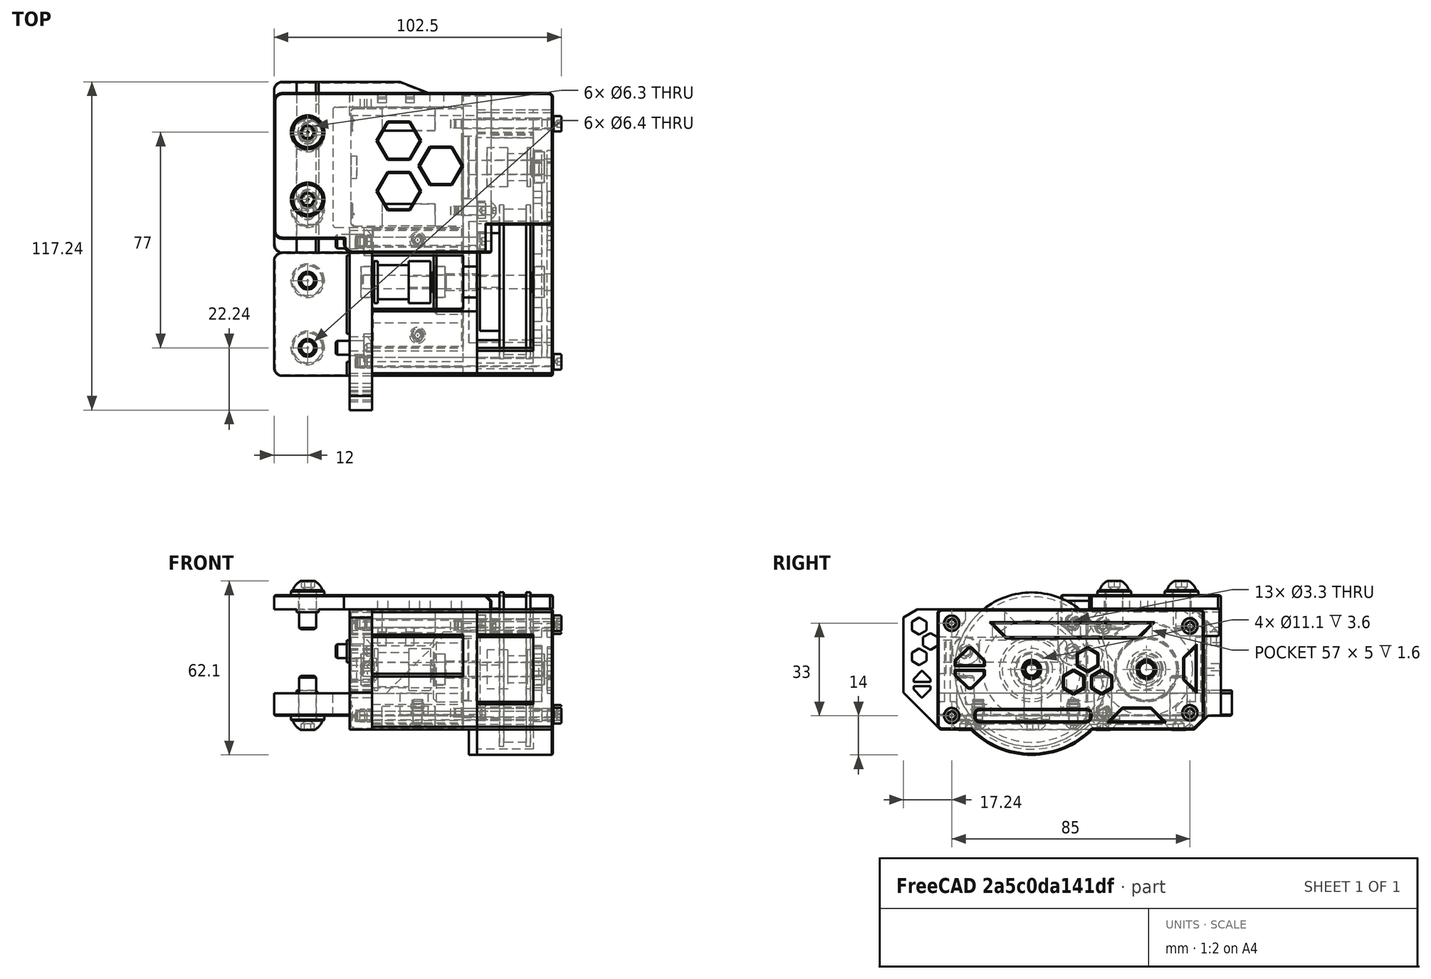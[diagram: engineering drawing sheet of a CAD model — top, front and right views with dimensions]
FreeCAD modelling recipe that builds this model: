
FCSTD DOCUMENT  (FreeCAD 0.19R24291 (Git))
Label: z-motor-left-assembly
License: Other
LicenseURL: GPL3
objects: Part::FeaturePython×28, Part::Feature×18, PartDesign::CoordinateSystem×1, App::Part×1
note: 47 computed .brp shape members not serialized (recipe doc carries the construction recipe); baked Part::Feature solids carry a one-line shape summary decoded from their .brp

FEATURE [Part::Feature] Part__Mirroring014002  label="motor-spacer"
  shape: bbox 0.5 x 6.9 x 6.9 mm, 4 faces (baked)
FEATURE [Part::Feature] Part__Mirroring002001  label="MR115ZZ006"
  shape: bbox 4 x 11 x 11 mm, 4 faces (baked)
FEATURE [Part::Feature] Part__Mirroring004001  label="20t-9mm-pulley001"
  shape: bbox 20 x 15 x 15 mm, 8 faces (baked)
FEATURE [Part::Feature] Part__Mirroring005001  label="MR115ZZ005"
  shape: bbox 4 x 11 x 11 mm, 4 faces (baked)
FEATURE [Part::Feature] Part__Mirroring007001  label="motor-spacer001"
  shape: bbox 0.5 x 6.9 x 6.9 mm, 4 faces (baked)
FEATURE [Part::Feature] Part__Mirroring008001  label="MR115ZZ007"
  shape: bbox 4 x 11 x 11 mm, 4 faces (baked)
FEATURE [Part::Feature] Part__Mirroring009001  label="motor-40mm001"
  shape: bbox 67 x 47 x 42 mm, 100 faces (baked)
FEATURE [Part::Feature] Part__Mirroring011001  label="motor-spacer002"
  shape: bbox 0.5 x 6.9 x 6.9 mm, 4 faces (baked)
FEATURE [Part::Feature] Part__Mirroring012001  label="motor-spacer003"
  shape: bbox 0.5 x 6.9 x 6.9 mm, 4 faces (baked)
FEATURE [Part::Feature] Part__Mirroring014001  label="16t-pulley001"
  shape: bbox 15.5 x 13.9 x 13.9 mm, 8 faces (baked)
FEATURE [Part::FeaturePython] Screw  label="M3x70-Screw"  # Fasteners workbench fastener (typed FeaturePython)
  Placement = pos=(72.5,-69.5,25) rot=(0,1,0;1.5708rad)
  diameter = 4
  invert = true
  length = 10
  lengthCustom = 70
  matchOuter = true
  offset = 0
  thread = false
  type = 33
FEATURE [Part::FeaturePython] Screw001  label="M3x70-Screw001"  # Fasteners workbench fastener (typed FeaturePython)
  Placement = pos=(72.5,-69.5,-8) rot=(0,1,0;1.5708rad)
  diameter = 4
  invert = true
  length = 10
  lengthCustom = 70
  matchOuter = true
  offset = 0
  thread = false
  type = 33
FEATURE [Part::FeaturePython] Screw002  label="M3x35-Screw"  # Fasteners workbench fastener (typed FeaturePython)
  Placement = pos=(72.5,15.5,24) rot=(0,1,0;1.5708rad)
  diameter = 4
  invert = true
  length = 10
  lengthCustom = 35
  matchOuter = true
  offset = 0
  thread = false
  type = 33
FEATURE [Part::FeaturePython] Screw003  label="M3x35-Screw001"  # Fasteners workbench fastener (typed FeaturePython)
  Placement = pos=(72.5,15.5,-7) rot=(0,1,0;1.5708rad)
  diameter = 4
  invert = true
  length = 10
  lengthCustom = 35
  matchOuter = true
  offset = 0
  thread = false
  type = 33
FEATURE [Part::FeaturePython] Screw004  label="M3x12-Screw"  # Fasteners workbench fastener (typed FeaturePython)
  Placement = pos=(50.5,-15.5,24) rot=(0,1,0;1.5708rad)
  diameter = 1
  invert = true
  length = 9
  lengthCustom = 12
  matchOuter = true
  offset = 0
  thread = false
  type = 39
FEATURE [Part::FeaturePython] Screw005  label="M3x8-Screw"  # Fasteners workbench fastener (typed FeaturePython)
  Placement = pos=(45.5,-15.5,-7) rot=(0,1,0;1.5708rad)
  diameter = 4
  invert = true
  length = 10
  lengthCustom = 8
  matchOuter = true
  offset = 0
  thread = false
  type = 33
FEATURE [Part::FeaturePython] Screw006  label="M5x10-Screw"  # Fasteners workbench fastener (typed FeaturePython)
  Placement = pos=(5,-64.5,15) rot=(0,1,0;1.5708rad)
  diameter = 3
  invert = true
  length = 12
  lengthCustom = 10
  matchOuter = true
  offset = 0
  thread = false
  type = 39
FEATURE [Part::FeaturePython] Screw007  label="M5x10-Screw001"  # Fasteners workbench fastener (typed FeaturePython)
  Placement = pos=(5,-26.5,15) rot=(0,1,0;1.5708rad)
  diameter = 3
  invert = true
  length = 12
  lengthCustom = 10
  matchOuter = true
  offset = 0
  thread = false
  type = 39
FEATURE [Part::FeaturePython] Washer  label="M6-Washer"  # Fasteners workbench fastener (typed FeaturePython)
  Placement = pos=(-15,-64.5,-8) rot=(1,0,0;3.14159rad)
  diameter = 2
  invert = false
  matchOuter = true
  offset = 0
  type = 4
FEATURE [Part::FeaturePython] Washer001  label="M6-Washer010"  # Fasteners workbench fastener (typed FeaturePython)
  Placement = pos=(-15,-40.5,-8) rot=(1,0,0;3.14159rad)
  diameter = 2
  invert = false
  matchOuter = true
  offset = 0
  type = 4
FEATURE [Part::FeaturePython] Washer002  label="M6-Washer006"  # Fasteners workbench fastener (typed FeaturePython)
  Placement = pos=(-15,-15.5,-8) rot=(1,0,0;3.14159rad)
  diameter = 2
  invert = false
  matchOuter = true
  offset = 0
  type = 4
FEATURE [Part::FeaturePython] Washer003  label="M6-Washer007"  # Fasteners workbench fastener (typed FeaturePython)
  Placement = pos=(-15,11.5,-8) rot=(1,0,0;3.14159rad)
  diameter = 2
  invert = false
  matchOuter = true
  offset = 0
  type = 4
FEATURE [Part::FeaturePython] Washer004  label="M6-Washer009"  # Fasteners workbench fastener (typed FeaturePython)
  Placement = pos=(-15,-11.5,35) rot=(0,0,1;0rad)
  diameter = 2
  invert = true
  matchOuter = true
  offset = 0
  type = 4
FEATURE [Part::FeaturePython] Washer005  label="M6-Washer008"  # Fasteners workbench fastener (typed FeaturePython)
  Placement = pos=(-15,12.5,35) rot=(0,0,1;0rad)
  diameter = 2
  invert = true
  matchOuter = true
  offset = 0
  type = 4
FEATURE [Part::FeaturePython] Screw008  label="M6x14-Screw"  # Fasteners workbench fastener (typed FeaturePython)
  Placement = pos=(-15,-11.5,36.8) rot=(0,0,1;0rad)
  baseObject = -> Washer004 [Edge1]
  diameter = 4
  invert = false
  length = 2
  lengthCustom = 14
  matchOuter = true
  offset = 0
  thread = false
  type = 39
FEATURE [Part::FeaturePython] Screw009  label="M6x14-Screw001"  # Fasteners workbench fastener (typed FeaturePython)
  Placement = pos=(-15,12.5,36.8) rot=(0,0,1;0rad)
  baseObject = -> Washer005 [Edge1]
  diameter = 4
  invert = false
  length = 2
  lengthCustom = 14
  matchOuter = true
  offset = 0
  thread = false
  type = 39
FEATURE [Part::FeaturePython] Screw010  label="M6x16-Screw"  # Fasteners workbench fastener (typed FeaturePython)
  Placement = pos=(-15,11.5,-9.8) rot=(1,0,0;3.14159rad)
  baseObject = -> Washer003 [Edge1]
  diameter = 4
  invert = false
  length = 3
  lengthCustom = 16
  matchOuter = true
  offset = 0
  thread = false
  type = 39
FEATURE [Part::FeaturePython] Screw011  label="M6x16-Screw001"  # Fasteners workbench fastener (typed FeaturePython)
  Placement = pos=(-15,-15.5,-9.8) rot=(1,0,0;3.14159rad)
  baseObject = -> Washer002 [Edge1]
  diameter = 4
  invert = false
  length = 3
  lengthCustom = 16
  matchOuter = true
  offset = 0
  thread = false
  type = 39
FEATURE [Part::FeaturePython] Screw012  label="M6x16-Screw005"  # Fasteners workbench fastener (typed FeaturePython)
  Placement = pos=(-15,-40.5,-9.8) rot=(1,0,0;3.14159rad)
  baseObject = -> Washer001 [Edge1]
  diameter = 4
  invert = false
  length = 3
  lengthCustom = 16
  matchOuter = true
  offset = 0
  thread = false
  type = 39
FEATURE [Part::FeaturePython] Screw013  label="M6x16-Screw004"  # Fasteners workbench fastener (typed FeaturePython)
  Placement = pos=(-15,-64.5,-9.8) rot=(1,0,0;3.14159rad)
  baseObject = -> Washer [Edge1]
  diameter = 4
  invert = false
  length = 3
  lengthCustom = 16
  matchOuter = true
  offset = 0
  thread = false
  type = 39
FEATURE [Part::FeaturePython] Screw014  label="M3x40-Screw"  # Fasteners workbench fastener (typed FeaturePython)
  Placement = pos=(45.5,-26.5,25) rot=(0,1,0;1.5708rad)
  diameter = 4
  invert = true
  length = 10
  lengthCustom = 40
  matchOuter = true
  offset = 0
  thread = false
  type = 33
FEATURE [Part::Feature] Cut001003001  label="80t-idler"
  Placement = pos=(64.5,-41,8.5) rot=(0,-1,0;1.5708rad)
  shape: bbox 18 x 55 x 55 mm, 10 faces (baked)
FEATURE [Part::Feature] Body002  label="5x65-shaft"
  Placement = pos=(4.5,-41,8.5) rot=(0,0,1;0rad)
  shape: bbox 65 x 5 x 5 mm, 11 faces (baked)
FEATURE [Part::Feature] Part__Mirroring014004009  label="MR115ZZ008"
  Placement = pos=(-26,0,0) rot=(0,0,1;0rad)
  shape: bbox 4 x 11 x 11 mm, 4 faces (baked)
FEATURE [Part::FeaturePython] HeatSet  label="M3x4-HeatSet"  # WARN: FeaturePython — macro-defined, semantics opaque (R4)
  Placement = pos=(8,-69.5,-8) rot=(0,1,0;1.5708rad)
  diameter = 2
  invert = true
  offset = 0
FEATURE [Part::FeaturePython] HeatSet001  label="M3x4-HeatSet001"  # WARN: FeaturePython — macro-defined, semantics opaque (R4)
  Placement = pos=(8,-69.5,25) rot=(0,1,0;1.5708rad)
  diameter = 2
  invert = true
  offset = 0
FEATURE [Part::FeaturePython] HeatSet002  label="M3x4-HeatSet002"  # WARN: FeaturePython — macro-defined, semantics opaque (R4)
  Placement = pos=(8,-26.5,25) rot=(0,1,0;1.5708rad)
  diameter = 2
  invert = true
  offset = 0
FEATURE [PartDesign::CoordinateSystem] LCS_z_motor_left  label="LCS_z-motor-left"
  AttacherType = Attacher::AttachEngine3D
FEATURE [Part::FeaturePython] HeatSet003  label="M3x3-HeatSet"  # WARN: FeaturePython — macro-defined, semantics opaque (R4)
  Placement = pos=(24.25,-26,-8) rot=(1,0,0;3.14159rad)
  diameter = 2
  invert = false
  offset = 0
FEATURE [Part::FeaturePython] HeatSet004  label="M3x3-HeatSet001"  # WARN: FeaturePython — macro-defined, semantics opaque (R4)
  Placement = pos=(24.25,-60,-8) rot=(1,0,0;3.14159rad)
  diameter = 2
  invert = false
  offset = 0
FEATURE [Part::FeaturePython] Screw015  label="M3x6-Screw"  # Fasteners workbench fastener (typed FeaturePython)
  Placement = pos=(24.25,-26,-11) rot=(1,0,0;3.14159rad)
  diameter = 1
  invert = false
  length = 0
  lengthCustom = 6
  matchOuter = true
  offset = 0
  thread = false
  type = 40
FEATURE [Part::FeaturePython] Screw016  label="M3x6-Screw001"  # Fasteners workbench fastener (typed FeaturePython)
  Placement = pos=(24.25,-60,-11) rot=(1,0,0;3.14159rad)
  diameter = 1
  invert = false
  length = 0
  lengthCustom = 6
  matchOuter = true
  offset = 0
  thread = false
  type = 40
FEATURE [Part::Feature] Part__Mirroring001001  label="z-motor-front-plate-left"
  Placement = pos=(0,0,0) rot=(0,0,1;3.14159rad)
  shape: bbox 27 x 95 x 52 mm, 216 faces (baked)
FEATURE [Part::Feature] Part__Mirroring001002  label="bottom-left-cover"
  Placement = pos=(0,0,0) rot=(0,0,1;3.14159rad)
  shape: bbox 32.25 x 42.5 x 3 mm, 14 faces (baked)
FEATURE [Part::Feature] Part__Mirroring003  label="z-motor-back-plate-left"
  shape: bbox 35 x 65.24 x 43 mm, 88 faces (baked)
FEATURE [Part::Feature] Part__Mirroring014004013  label="z-motor-body-left"
  shape: bbox 72.5 x 105 x 52 mm, 105 faces (baked)
FEATURE [Part::Feature] Part__Mirroring001  label="z-motor-top-plate-left"
  shape: bbox 99.5 x 57 x 18 mm, 124 faces (baked)
FEATURE [App::Part] Part  label="z-motor-left"
  Group = -> [Part__Mirroring014002,Part__Mirroring002001,Part__Mirroring004001,Part__Mirroring005001,Part__Mirroring007001,Part__Mirroring008001,Part__Mirroring009001,Part__Mirroring011001,Part__Mirroring012001,Part__Mirroring014001,Screw002,Screw001,Screw003,Screw,Washer005,Washer004,Screw008,Screw009,Screw004,Washer002,Washer003,Screw010,Screw011,Screw005,Washer,Screw007,Washer001,Screw013,Screw012,Screw006,+17 more]
  Origin = -> Origin
